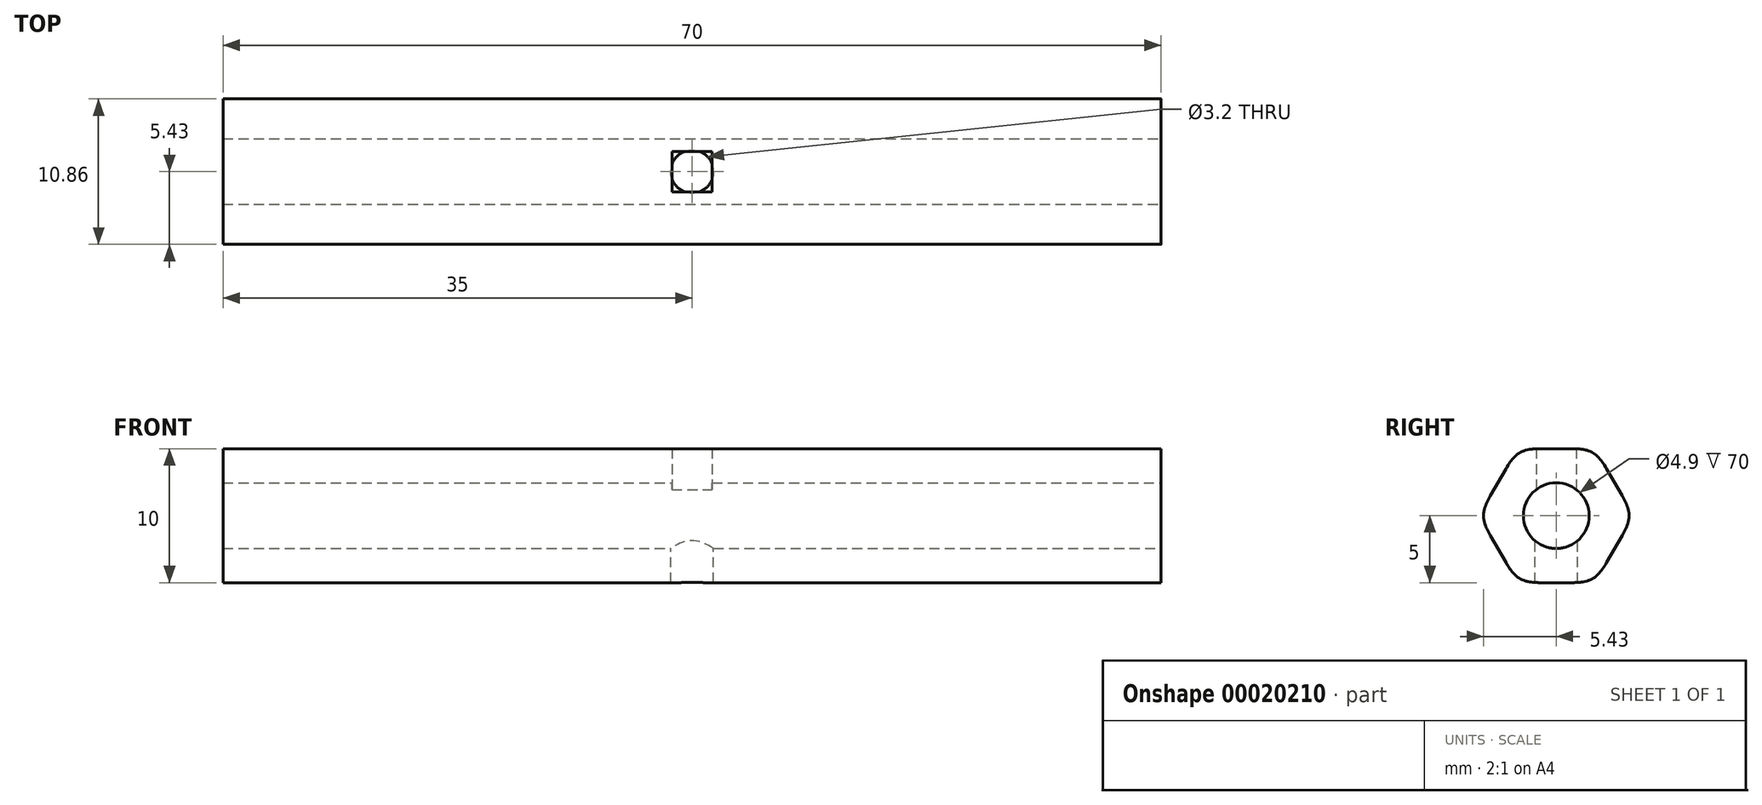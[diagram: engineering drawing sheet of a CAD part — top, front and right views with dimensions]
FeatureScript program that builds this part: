
annotation { "Feature Type Name" : "Feature", "Feature Type Description" : "" }
export const myFeature = defineFeature(function(context is Context, id is Id, definition is map)
    precondition{}
    {
        {
            var Q0;
            Q0=qCreatedBy(makeId("Right.planeOp"),FACE);
            var sketch = newSketch(context, id + "F0", { "sketchPlane" : qUnion([Q0])});
            skCircle(sketch, "E0", {"center": v(0, 0) * mm, "radius": 5 * mm, "construction": true});
            skLineSegment(sketch, "E1", {"start": v(-2.89, 5) * mm, "end": v(2.89, 5) * mm});
            skLineSegment(sketch, "E2", {"start": v(2.89, 5) * mm, "end": v(5.77, 0) * mm});
            skLineSegment(sketch, "E3", {"start": v(5.77, 0) * mm, "end": v(2.89, -5) * mm});
            skLineSegment(sketch, "E4", {"start": v(2.89, -5) * mm, "end": v(-2.89, -5) * mm});
            skLineSegment(sketch, "E5", {"start": v(-2.89, -5) * mm, "end": v(-5.77, 0) * mm});
            skLineSegment(sketch, "E6", {"start": v(-5.77, 0) * mm, "end": v(-2.89, 5) * mm});
            skSolve(sketch);
        }
        {
            var Q0;
            Q0=makeQuery(id+"F0.imprint","IMPRINT",FACE,{"disambiguationData":[TD([[makeQuery(id+"F0.imprint","IMPRINT",EDGE,{"derivedFrom":sQuery(id+"F0.wireOp",EDGE,"E1")}),-1.0]])]});
            extrude(context, id + "F1", {"entities" : qUnion([Q0]), "endBound" : BoundingType.SYMMETRIC, "depth" : 70 * mm});
        }
        {
            var Q0;
            Q0=makeQuery(id+"F1.opExtrude","CAP_FACE",FACE,{"disambiguationData":[OSD([sQuery(id+"F0.wireOp",EDGE,"E1"),sQuery(id+"F0.wireOp",EDGE,"E2"),sQuery(id+"F0.wireOp",EDGE,"E3"),sQuery(id+"F0.wireOp",EDGE,"E4"),sQuery(id+"F0.wireOp",EDGE,"E5"),sQuery(id+"F0.wireOp",EDGE,"E6")])],"isStart":false});
            var sketch = newSketch(context, id + "F2", { "sketchPlane" : qUnion([Q0])});
            skCircle(sketch, "E7", {"center": v(0, 0) * mm, "radius": 2.45 * mm});
            skSolve(sketch);
        }
        {
            var Q0;
            Q0 = qSketchRegion(id + "F2", true);
            extrude(context, id + "F3", {"entities" : qUnion([Q0]), "operationType" : NewBodyOperationType.REMOVE, "endBound" : BoundingType.THROUGH_ALL, "oppositeDirection" : true, "depth" : 25 * mm});
        }
        {
            var Q0;
            Q0=qCreatedBy(makeId("Top.planeOp"),FACE);
            var sketch = newSketch(context, id + "F4", { "sketchPlane" : qUnion([Q0])});
            skLineSegment(sketch, "E8.rect.bottom", {"start": v(-1.5, 1.5) * mm, "end": v(1.5, 1.5) * mm});
            skLineSegment(sketch, "E8.rect.top", {"start": v(-1.5, -1.5) * mm, "end": v(1.5, -1.5) * mm});
            skLineSegment(sketch, "E8.rect.left", {"start": v(-1.5, 1.5) * mm, "end": v(-1.5, -1.5) * mm});
            skLineSegment(sketch, "E8.rect.right", {"start": v(1.5, 1.5) * mm, "end": v(1.5, -1.5) * mm});
            skPoint(sketch, "E8.rect.middle", {"position": v(0, 0) * mm});
            skSolve(sketch);
        }
        {
            var Q0;
            Q0 = qSketchRegion(id + "F4", true);
            var Q1;
            Q1=makeQuery(id+"F1.opExtrude","SWEPT_FACE",FACE,{"disambiguationData":[OSD([sQuery(id+"F0.wireOp",EDGE,"E1")])]});
            extrude(context, id + "F5", {"entities" : qUnion([Q0]), "operationType" : NewBodyOperationType.REMOVE, "endBound" : BoundingType.THROUGH_ALL, "endBoundEntityFace" : qUnion([Q1]), "depth" : 12 * mm});
        }
        {
            var Q0;
            Q0=makeQuery(id+"F1.opExtrude","SWEPT_EDGE",EDGE,{"disambiguationData":[OSD([sQuery(id+"F0.wireOp",EDGE,"E1"),sQuery(id+"F0.wireOp",EDGE,"E6")])]});
            var Q1;
            Q1=makeQuery(id+"F1.opExtrude","SWEPT_EDGE",EDGE,{"disambiguationData":[OSD([sQuery(id+"F0.wireOp",EDGE,"E1"),sQuery(id+"F0.wireOp",EDGE,"E2")])]});
            var Q2;
            Q2=makeQuery(id+"F1.opExtrude","SWEPT_EDGE",EDGE,{"disambiguationData":[OSD([sQuery(id+"F0.wireOp",EDGE,"E2"),sQuery(id+"F0.wireOp",EDGE,"E3")])]});
            var Q3;
            Q3=makeQuery(id+"F1.opExtrude","SWEPT_EDGE",EDGE,{"disambiguationData":[OSD([sQuery(id+"F0.wireOp",EDGE,"E5"),sQuery(id+"F0.wireOp",EDGE,"E6")])]});
            var Q4;
            Q4=makeQuery(id+"F1.opExtrude","SWEPT_EDGE",EDGE,{"disambiguationData":[OSD([sQuery(id+"F0.wireOp",EDGE,"E3"),sQuery(id+"F0.wireOp",EDGE,"E4")])]});
            var Q5;
            Q5=makeQuery(id+"F1.opExtrude","SWEPT_EDGE",EDGE,{"disambiguationData":[OSD([sQuery(id+"F0.wireOp",EDGE,"E4"),sQuery(id+"F0.wireOp",EDGE,"E5")])]});
            fillet(context, id + "F6", {"entities" : qUnion([Q0, Q1, Q2, Q3, Q4, Q5]), "radius" : 3 * mm, "tangentPropagation" : true, "rho" : .6, "crossSection" : FilletCrossSection.CONIC, "allowEdgeOverflow" : false});
        }
        {
            var Q0;
            Q0=qCreatedBy(makeId("Top.planeOp"),FACE);
            var sketch = newSketch(context, id + "F7", { "sketchPlane" : qUnion([Q0])});
            skCircle(sketch, "E9", {"center": v(0, 0) * mm, "radius": 1.6 * mm});
            skSolve(sketch);
        }
        {
            var Q0;
            Q0 = qSketchRegion(id + "F7", true);
            extrude(context, id + "F8", {"entities" : qUnion([Q0]), "operationType" : NewBodyOperationType.REMOVE, "endBound" : BoundingType.THROUGH_ALL, "oppositeDirection" : true, "depth" : 25 * mm});
        }
    });
